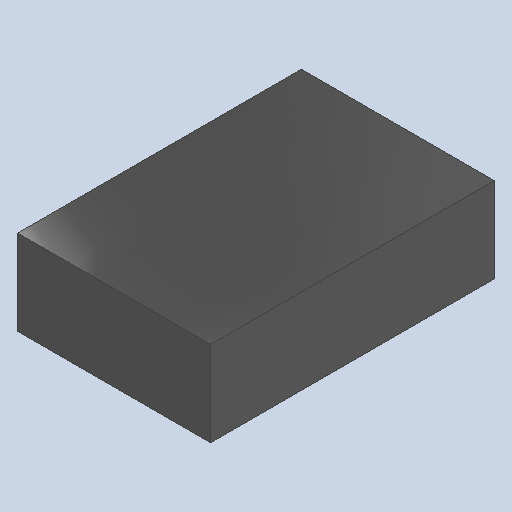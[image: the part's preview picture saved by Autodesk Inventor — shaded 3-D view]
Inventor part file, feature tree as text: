
AUTODESK INVENTOR PART (.ipt)
format: ipt  version: 2025.2 (Build 292293000, 293)  size: 90,112 bytes
history: native  units: mm
features: extrude x1, sketch x1
ambient origin geometry x8: Origin, YZ Plane, XZ Plane, XY Plane, X Axis, Y Axis, Z Axis, Center Point
bodies: Solid1 (feature_tree)
feature tree (2):
  extrude  "Extrusion1"  Depth=50.0mm
  sketch  "Sketch1"  dims[d0=34.0mm d1=50.0mm d2=15.0mm d3=0.0mm]
